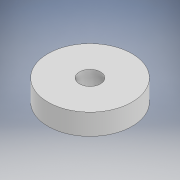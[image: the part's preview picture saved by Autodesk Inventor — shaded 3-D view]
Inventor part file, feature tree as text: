
AUTODESK INVENTOR PART (.ipt)
format: ipt  version: 2020 (Build 240168000, 168)  size: 96,256 bytes
history: native  units: mm
features: extrude x1, sketch x1
ambient origin geometry x8: Origin, YZ Plane, XZ Plane, XY Plane, X Axis, Y Axis, Z Axis, Center Point
bodies: Solid1 (feature_tree)
feature tree (2):
  extrude  "Extrusion1"  Depth=5.0mm
  sketch  "Sketch1"  dims[d0=20.0mm d1=5.0mm d2=5.0mm d3=0.0mm d4=0.872665mm]
